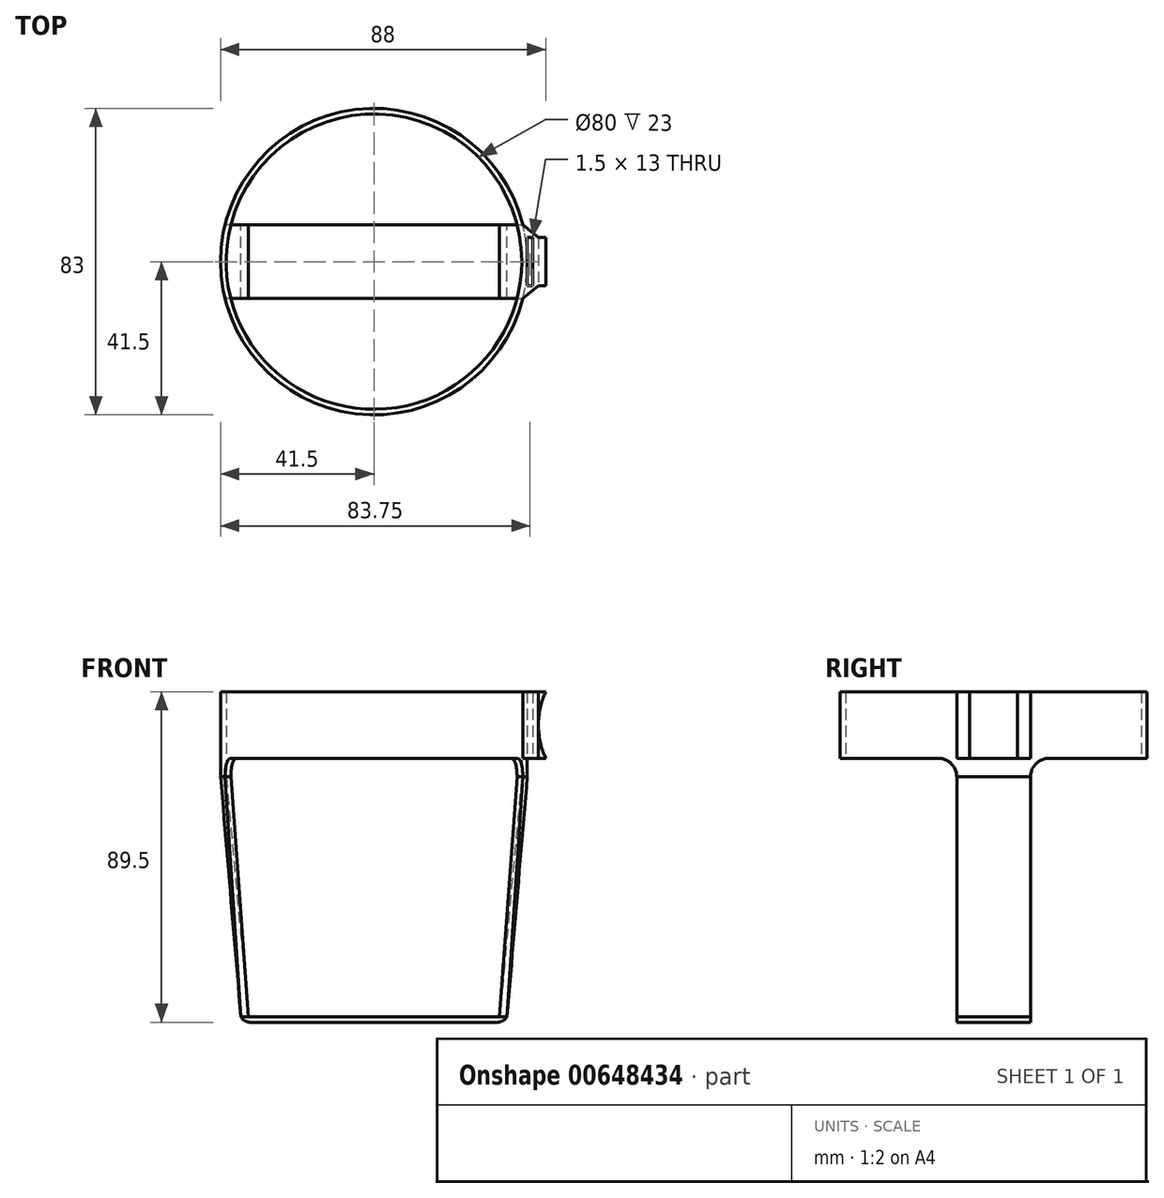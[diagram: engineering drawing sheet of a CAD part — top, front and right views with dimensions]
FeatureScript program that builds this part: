
annotation { "Feature Type Name" : "Feature", "Feature Type Description" : "" }
export const myFeature = defineFeature(function(context is Context, id is Id, definition is map)
    precondition{}
    {
        {
            var Q0;
            Q0=qCreatedBy(makeId("Top.planeOp"),FACE);
            var sketch = newSketch(context, id + "F0", { "sketchPlane" : qUnion([Q0])});
            skCircle(sketch, "E0", {"center": v(0, 0) * mm, "radius": 40 * mm});
            skCircle(sketch, "E1.0", {"center": v(0, 0) * mm, "radius": 41.5 * mm});
            skLineSegment(sketch, "E2", {"start": v(-40, 0) * mm, "end": v(40, 0) * mm, "construction": true});
            skLineSegment(sketch, "E3.bottom", {"start": v(36, -10) * mm, "end": v(-36, -10) * mm});
            skLineSegment(sketch, "E3.top", {"start": v(36, 10) * mm, "end": v(-36, 10) * mm});
            skLineSegment(sketch, "E3.left", {"start": v(36, -10) * mm, "end": v(36, 10) * mm});
            skLineSegment(sketch, "E3.right", {"start": v(-36, -10) * mm, "end": v(-36, 10) * mm});
            skPoint(sketch, "E4.startSnap0", {"position": v(36, 0) * mm});
            skLineSegment(sketch, "E5", {"start": v(41.5, 6.5) * mm, "end": v(41.5, -6.5) * mm});
            skPoint(sketch, "E6", {"position": v(41.5, 0) * mm});
            skLineSegment(sketch, "E7", {"start": v(41.5, -6.5) * mm, "end": v(43, -6.5) * mm});
            skLineSegment(sketch, "E8", {"start": v(41.5, 6.5) * mm, "end": v(43, 6.5) * mm});
            skLineSegment(sketch, "E9", {"start": v(43, -6.5) * mm, "end": v(43, 6.5) * mm});
            skLineSegment(sketch, "E10", {"start": v(36, -10) * mm, "end": v(50.55, -10) * mm});
            skLineSegment(sketch, "E11", {"start": v(36, 10) * mm, "end": v(53.17, 10) * mm});
            skLineSegment(sketch, "E12.0", {"start": v(44.5, -6.5) * mm, "end": v(44.5, 6.5) * mm});
            skLineSegment(sketch, "E13", {"start": v(40.28, 10) * mm, "end": v(44.5, 6.5) * mm});
            skLineSegment(sketch, "E14", {"start": v(44.5, -6.5) * mm, "end": v(40.28, -10) * mm});
            skLineSegment(sketch, "E15", {"start": v(-36, 10) * mm, "end": v(-40.28, 10) * mm});
            skLineSegment(sketch, "E16", {"start": v(-36, -10) * mm, "end": v(-40.28, -10) * mm});
            skSolve(sketch);
        }
        {
            var Q0;
            Q0=makeQuery(id+"F0.imprint","IMPRINT",FACE,{"disambiguationData":[TD([[makeQuery(id+"F0.imprint","IMPRINT",EDGE,{"derivedFrom":sQuery(id+"F0.wireOp",EDGE,"E0")}),-1.0]])]});
            var Q1;
            {var subQ0=sQuery(id+"F0.wireOp",EDGE,"E7");Q1=makeQuery(id+"F0.imprint","IMPRINT",FACE,{"disambiguationData":[TD([[makeQuery(id+"F0.imprint","IMPRINT",EDGE,{"derivedFrom":subQ0}),-1.0]])]});}
            var Q2;
            {var subQ3=sQuery(id+"F0.wireOp",EDGE,"E0");var subQ6=sQuery(id+"F0.wireOp",EDGE,"E11");var subQ8=makeQuery(id+"F0.imprint","INTERSECT",VERTEX,{"derivedFrom":[subQ3,subQ6]});Q2=makeQuery(id+"F0.imprint","IMPRINT",FACE,{"disambiguationData":[TD([[makeQuery(id+"F0.imprint","IMPRINT",EDGE,{"disambiguationData":[TD([[subQ8,1.0]])],"derivedFrom":subQ3}),-1.0]])]});}
            extrude(context, id + "F1", {"entities" : qUnion([Q0, Q1, Q2]), "depth" : 18 * mm, "offsetDistance" : 25 * mm});
        }
        {
            var Q0;
            Q0=makeQuery(id+"F0.imprint","IMPRINT",FACE,{"disambiguationData":[TD([[makeQuery(id+"F0.imprint","IMPRINT",EDGE,{"derivedFrom":sQuery(id+"F0.wireOp",EDGE,"E3.bottom")}),-1.0]])]});
            extrude(context, id + "F2", {"entities" : qUnion([Q0]), "oppositeDirection" : true, "depth" : 1.5 * mm, "hasOffset" : true, "offsetDistance" : 25 * mm});
        }
        {
            var Q0;
            Q0=makeQuery(id+"F2.opExtrude","SWEPT_BODY",BODY,{"disambiguationData":[OSD([sQuery(id+"F0.wireOp",EDGE,"E3.bottom"),sQuery(id+"F0.wireOp",EDGE,"E3.top"),sQuery(id+"F0.wireOp",EDGE,"E3.left"),sQuery(id+"F0.wireOp",EDGE,"E3.right")])]});
            transform(context, id + "F3", {"entities" : qUnion([Q0]), "transformType" : TransformType.TRANSLATION_3D, "dx" : 0 * mm, "dy" : 0 * mm, "dz" : -70 * mm, "makeCopy" : false});
        }
        {
            var Q0;
            Q0=makeQuery(id+"F2.opExtrude","CAP_FACE",FACE,{"disambiguationData":[OSD([sQuery(id+"F0.wireOp",EDGE,"E3.bottom"),sQuery(id+"F0.wireOp",EDGE,"E3.top"),sQuery(id+"F0.wireOp",EDGE,"E3.left"),sQuery(id+"F0.wireOp",EDGE,"E3.right")])],"isStart":true});
            var sketch = newSketch(context, id + "F4", { "sketchPlane" : qUnion([Q0])});
            skLineSegment(sketch, "E17", {"start": v(-34, 10) * mm, "end": v(-34, -10) * mm});
            skLineSegment(sketch, "E18", {"start": v(34, 10) * mm, "end": v(34, -10) * mm});
            skSolve(sketch);
        }
        {
            var Q0;
            {var subQ0=sQuery(id+"F0.wireOp",EDGE,"E15");var subQ1=sQuery(id+"F0.wireOp",EDGE,"E0");var subQ2=makeQuery(id+"F0.imprint","INTERSECT",VERTEX,{"derivedFrom":[subQ1,subQ0]});Q0=makeQuery(id+"F0.imprint","IMPRINT",FACE,{"disambiguationData":[TD([[makeQuery(id+"F0.imprint","IMPRINT",EDGE,{"disambiguationData":[TD([[subQ2,-1.0]])],"derivedFrom":subQ1}),-1.0]])]});}
            var Q1;
            {var subQ3=sQuery(id+"F0.wireOp",EDGE,"E0");var subQ6=sQuery(id+"F0.wireOp",EDGE,"E11");var subQ8=makeQuery(id+"F0.imprint","INTERSECT",VERTEX,{"derivedFrom":[subQ3,subQ6]});Q1=makeQuery(id+"F0.imprint","IMPRINT",FACE,{"disambiguationData":[TD([[makeQuery(id+"F0.imprint","IMPRINT",EDGE,{"disambiguationData":[TD([[subQ8,1.0]])],"derivedFrom":subQ3}),-1.0]])]});}
            extrude(context, id + "F5", {"entities" : qUnion([Q0, Q1]), "operationType" : NewBodyOperationType.ADD, "oppositeDirection" : true, "depth" : 5 * mm, "offsetDistance" : 25 * mm});
        }
        {
            var Q0;
            Q0=makeQuery(id+"F5.opExtrude","CAP_EDGE",EDGE,{"disambiguationData":[OSD([sQuery(id+"F0.wireOp",EDGE,"E16")])],"isStart":true});
            var Q1;
            Q1=makeQuery(id+"F5.opExtrude","CAP_EDGE",EDGE,{"disambiguationData":[OSD([sQuery(id+"F0.wireOp",EDGE,"E15")])],"isStart":true});
            var Q2;
            Q2=makeQuery(id+"F5.opExtrude","CAP_EDGE",EDGE,{"disambiguationData":[OSD([sQuery(id+"F0.wireOp",EDGE,"E10")])],"isStart":true});
            var Q3;
            Q3=makeQuery(id+"F5.opExtrude","CAP_EDGE",EDGE,{"disambiguationData":[OSD([sQuery(id+"F0.wireOp",EDGE,"E11")])],"isStart":true});
            fillet(context, id + "F6", {"entities" : qUnion([Q0, Q1, Q2, Q3]), "radius" : 5 * mm, "tangentPropagation" : true, "allowEdgeOverflow" : false});
        }
        {
            var Q0;
            {var subQ0=sQuery(id+"F4.wireOp",EDGE,"E17");Q0=makeQuery(id+"F4.imprint","IMPRINT",FACE,{"disambiguationData":[TD([[makeQuery(id+"F4.imprint","IMPRINT",EDGE,{"derivedFrom":subQ0}),-1.0]])]});}
            var Q1;
            Q1=makeQuery(id+"F5.opExtrude","CAP_FACE",FACE,{"disambiguationData":[OSD([sQuery(id+"F0.wireOp",EDGE,"E0"),sQuery(id+"F0.wireOp",EDGE,"E1.0"),sQuery(id+"F0.wireOp",EDGE,"E15"),sQuery(id+"F0.wireOp",EDGE,"E16")])],"isStart":false});
            loft(context, id + "F7", {"sheetProfilesArray" : [{ "sheetProfileEntities" : qUnion([Q0]) }, { "sheetProfileEntities" : qUnion([Q1]) }]});
        }
        {
            var Q0;
            {var subQ0=sQuery(id+"F4.wireOp",EDGE,"E18");Q0=makeQuery(id+"F4.imprint","IMPRINT",FACE,{"disambiguationData":[TD([[makeQuery(id+"F4.imprint","IMPRINT",EDGE,{"derivedFrom":subQ0}),1.0]])]});}
            var Q1;
            Q1=makeQuery(id+"F5.opExtrude","CAP_FACE",FACE,{"disambiguationData":[OSD([sQuery(id+"F0.wireOp",EDGE,"E0"),sQuery(id+"F0.wireOp",EDGE,"E1.0"),sQuery(id+"F0.wireOp",EDGE,"E10"),sQuery(id+"F0.wireOp",EDGE,"E11")])],"isStart":false});
            loft(context, id + "F8", {"sheetProfilesArray" : [{ "sheetProfileEntities" : qUnion([Q0]) }, { "sheetProfileEntities" : qUnion([Q1]) }]});
        }
        {
            var Q0;
            Q0=makeQuery(id+"F2.opExtrude","CAP_EDGE",EDGE,{"disambiguationData":[OSD([sQuery(id+"F0.wireOp",EDGE,"E3.left")])],"isStart":false});
            var Q1;
            Q1=makeQuery(id+"F2.opExtrude","CAP_EDGE",EDGE,{"disambiguationData":[OSD([sQuery(id+"F0.wireOp",EDGE,"E3.right")])],"isStart":false});
            fillet(context, id + "F9", {"entities" : qUnion([Q0, Q1]), "radius" : 3 * mm, "tangentPropagation" : true, "allowEdgeOverflow" : false});
        }
        {
            var Q0;
            Q0=makeQuery(id+"F1.opExtrude","SWEPT_FACE",FACE,{"disambiguationData":[OSD([sQuery(id+"F0.wireOp",EDGE,"E12.0")])]});
            extrude(context, id + "F10", {"entities" : qUnion([Q0]), "operationType" : NewBodyOperationType.ADD, "depth" : 2 * mm, "offsetDistance" : 25 * mm});
        }
        {
            var Q0;
            Q0=makeQuery(id+"F10.opExtrude","SWEPT_FACE",FACE,{"disambiguationData":[OSD([sQuery(id+"F0.wireOp",EDGE,"E12.0"),sQuery(id+"F0.wireOp",EDGE,"E14")])]});
            var sketch = newSketch(context, id + "F11", { "sketchPlane" : qUnion([Q0])});
            skArc(sketch, "E19", {"start": v(46.5, 18) * mm, "mid": v(44.5, 9) * mm, "end": v(46.5, 0) * mm});
            skSolve(sketch);
        }
        {
            var Q0;
            {var subQ1=sQuery(id+"F0.wireOp",EDGE,"E14");var subQ2=sQuery(id+"F0.wireOp",EDGE,"E12.0");var subQ3=makeQuery(id+"F10.opExtrude","CAP_EDGE",EDGE,{"disambiguationData":[OSD([subQ2,subQ1])],"isStart":false});Q0=makeQuery(id+"F11.imprint","IMPRINT",FACE,{"disambiguationData":[TD([[makeQuery(id+"F11.imprint","IMPRINT",EDGE,{"derivedFrom":subQ3}),-1.0]])]});}
            extrude(context, id + "F12", {"entities" : qUnion([Q0]), "operationType" : NewBodyOperationType.REMOVE, "endBound" : BoundingType.THROUGH_ALL, "oppositeDirection" : true, "depth" : 25 * mm, "offsetDistance" : 25 * mm});
        }
    });
